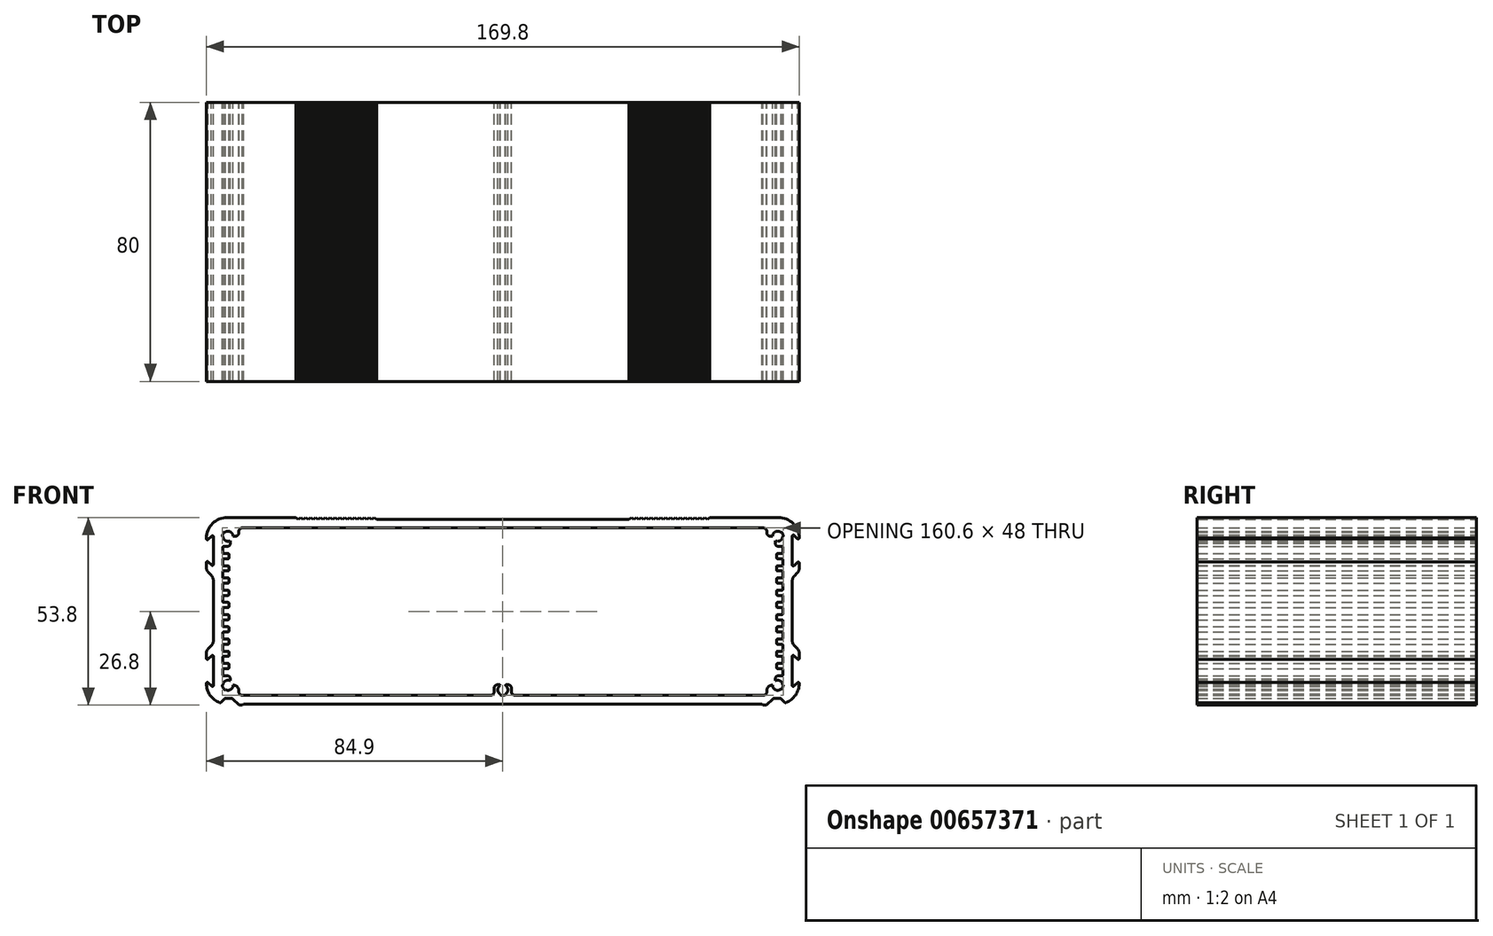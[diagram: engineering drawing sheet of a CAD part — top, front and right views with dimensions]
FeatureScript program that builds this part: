
annotation { "Feature Type Name" : "Feature", "Feature Type Description" : "" }
export const myFeature = defineFeature(function(context is Context, id is Id, definition is map)
    precondition{}
    {
        {
            var Q0;
            Q0=qCreatedBy(makeId("Front.planeOp"),FACE);
            var sketch = newSketch(context, id + "F0", { "sketchPlane" : qUnion([Q0])});
            skArc(sketch, "E0", {"start": v(-74.6, 23.9) * mm, "mid": v(-75.3, 23.6) * mm, "end": v(-75.6, 22.9) * mm});
            skLineSegment(sketch, "E1", {"start": v(74.6, 23.9) * mm, "end": v(-74.6, 23.9) * mm});
            skArc(sketch, "E2", {"start": v(75.6, 22.9) * mm, "mid": v(75.3, 23.6) * mm, "end": v(74.6, 23.9) * mm});
            skLineSegment(sketch, "E3", {"start": v(75.6, 22.5) * mm, "end": v(75.6, 22.9) * mm});
            skArc(sketch, "E4", {"start": v(75.6, 22.5) * mm, "mid": v(75.9, 21.8) * mm, "end": v(76.6, 21.5) * mm});
            skLineSegment(sketch, "E5", {"start": v(77.25, 21.5) * mm, "end": v(76.6, 21.5) * mm});
            skArc(sketch, "E6", {"start": v(79.64, 22.6) * mm, "mid": v(78.1, 22.82) * mm, "end": v(77.25, 21.5) * mm});
            skLineSegment(sketch, "E7", {"start": v(79.73, 22.73) * mm, "end": v(79.64, 22.6) * mm});
            skArc(sketch, "E8", {"start": v(80.3, 21.5) * mm, "mid": v(80.15, 22.18) * mm, "end": v(79.73, 22.73) * mm});
            skLineSegment(sketch, "E9", {"start": v(80.15, 21.5) * mm, "end": v(80.3, 21.5) * mm});
            skArc(sketch, "E10", {"start": v(78.03, 20.22) * mm, "mid": v(79.45, 20.26) * mm, "end": v(80.15, 21.5) * mm});
            skLineSegment(sketch, "E11", {"start": v(78.03, 19.52) * mm, "end": v(78.03, 20.22) * mm});
            skArc(sketch, "E12", {"start": v(78.03, 19.52) * mm, "mid": v(78.33, 18.83) * mm, "end": v(79.02, 18.55) * mm});
            skLineSegment(sketch, "E13", {"start": v(79.95, 18.55) * mm, "end": v(79.02, 18.55) * mm});
            skArc(sketch, "E14", {"start": v(80.25, 18.25) * mm, "mid": v(80.16, 18.46) * mm, "end": v(79.95, 18.55) * mm});
            skLineSegment(sketch, "E15", {"start": v(80.25, 16.85) * mm, "end": v(80.25, 18.25) * mm});
            skArc(sketch, "E16", {"start": v(79.95, 16.55) * mm, "mid": v(80.16, 16.64) * mm, "end": v(80.25, 16.85) * mm});
            skLineSegment(sketch, "E17", {"start": v(78.7, 16.55) * mm, "end": v(79.95, 16.55) * mm});
            skArc(sketch, "E18", {"start": v(78.7, 16.55) * mm, "mid": v(78.49, 16.46) * mm, "end": v(78.4, 16.25) * mm});
            skLineSegment(sketch, "E19", {"start": v(78.4, 15.35) * mm, "end": v(78.4, 16.25) * mm});
            skArc(sketch, "E20", {"start": v(78.4, 15.35) * mm, "mid": v(78.49, 15.14) * mm, "end": v(78.7, 15.05) * mm});
            skLineSegment(sketch, "E21", {"start": v(79.95, 15.05) * mm, "end": v(78.7, 15.05) * mm});
            skArc(sketch, "E22", {"start": v(80.25, 14.75) * mm, "mid": v(80.16, 14.96) * mm, "end": v(79.95, 15.05) * mm});
            skLineSegment(sketch, "E23", {"start": v(80.25, 13.35) * mm, "end": v(80.25, 14.75) * mm});
            skArc(sketch, "E24", {"start": v(79.95, 13.05) * mm, "mid": v(80.16, 13.14) * mm, "end": v(80.25, 13.35) * mm});
            skLineSegment(sketch, "E25", {"start": v(78.7, 13.05) * mm, "end": v(79.95, 13.05) * mm});
            skArc(sketch, "E26", {"start": v(78.7, 13.05) * mm, "mid": v(78.49, 12.96) * mm, "end": v(78.4, 12.75) * mm});
            skLineSegment(sketch, "E27", {"start": v(78.4, 11.85) * mm, "end": v(78.4, 12.75) * mm});
            skArc(sketch, "E28", {"start": v(78.4, 11.85) * mm, "mid": v(78.49, 11.64) * mm, "end": v(78.7, 11.55) * mm});
            skLineSegment(sketch, "E29", {"start": v(79.95, 11.55) * mm, "end": v(78.7, 11.55) * mm});
            skArc(sketch, "E30", {"start": v(80.25, 11.25) * mm, "mid": v(80.16, 11.46) * mm, "end": v(79.95, 11.55) * mm});
            skLineSegment(sketch, "E31", {"start": v(80.25, 9.85) * mm, "end": v(80.25, 11.25) * mm});
            skArc(sketch, "E32", {"start": v(79.95, 9.55) * mm, "mid": v(80.16, 9.64) * mm, "end": v(80.25, 9.85) * mm});
            skLineSegment(sketch, "E33", {"start": v(78.7, 9.55) * mm, "end": v(79.95, 9.55) * mm});
            skArc(sketch, "E34", {"start": v(78.7, 9.55) * mm, "mid": v(78.49, 9.46) * mm, "end": v(78.4, 9.25) * mm});
            skLineSegment(sketch, "E35", {"start": v(78.4, 8.35) * mm, "end": v(78.4, 9.25) * mm});
            skArc(sketch, "E36", {"start": v(78.4, 8.35) * mm, "mid": v(78.49, 8.14) * mm, "end": v(78.7, 8.05) * mm});
            skLineSegment(sketch, "E37", {"start": v(79.95, 8.05) * mm, "end": v(78.7, 8.05) * mm});
            skArc(sketch, "E38", {"start": v(80.25, 7.75) * mm, "mid": v(80.16, 7.96) * mm, "end": v(79.95, 8.05) * mm});
            skLineSegment(sketch, "E39", {"start": v(80.25, 6.35) * mm, "end": v(80.25, 7.75) * mm});
            skArc(sketch, "E40", {"start": v(79.95, 6.05) * mm, "mid": v(80.16, 6.14) * mm, "end": v(80.25, 6.35) * mm});
            skLineSegment(sketch, "E41", {"start": v(78.7, 6.05) * mm, "end": v(79.95, 6.05) * mm});
            skArc(sketch, "E42", {"start": v(78.7, 6.05) * mm, "mid": v(78.49, 5.96) * mm, "end": v(78.4, 5.75) * mm});
            skLineSegment(sketch, "E43", {"start": v(78.4, 4.85) * mm, "end": v(78.4, 5.75) * mm});
            skArc(sketch, "E44", {"start": v(78.4, 4.85) * mm, "mid": v(78.49, 4.64) * mm, "end": v(78.7, 4.55) * mm});
            skLineSegment(sketch, "E45", {"start": v(79.95, 4.55) * mm, "end": v(78.7, 4.55) * mm});
            skArc(sketch, "E46", {"start": v(80.25, 4.25) * mm, "mid": v(80.16, 4.46) * mm, "end": v(79.95, 4.55) * mm});
            skLineSegment(sketch, "E47", {"start": v(80.25, 2.85) * mm, "end": v(80.25, 4.25) * mm});
            skArc(sketch, "E48", {"start": v(79.95, 2.55) * mm, "mid": v(80.16, 2.64) * mm, "end": v(80.25, 2.85) * mm});
            skLineSegment(sketch, "E49", {"start": v(78.7, 2.55) * mm, "end": v(79.95, 2.55) * mm});
            skArc(sketch, "E50", {"start": v(78.7, 2.55) * mm, "mid": v(78.49, 2.46) * mm, "end": v(78.4, 2.25) * mm});
            skLineSegment(sketch, "E51", {"start": v(78.4, 1.35) * mm, "end": v(78.4, 2.25) * mm});
            skArc(sketch, "E52", {"start": v(78.4, 1.35) * mm, "mid": v(78.49, 1.14) * mm, "end": v(78.7, 1.05) * mm});
            skLineSegment(sketch, "E53", {"start": v(79.95, 1.05) * mm, "end": v(78.7, 1.05) * mm});
            skArc(sketch, "E54", {"start": v(80.25, 0.75) * mm, "mid": v(80.16, 0.96) * mm, "end": v(79.95, 1.05) * mm});
            skLineSegment(sketch, "E55", {"start": v(80.25, -0.65) * mm, "end": v(80.25, 0.75) * mm});
            skArc(sketch, "E56", {"start": v(79.95, -0.95) * mm, "mid": v(80.16, -0.86) * mm, "end": v(80.25, -0.65) * mm});
            skLineSegment(sketch, "E57", {"start": v(78.7, -0.95) * mm, "end": v(79.95, -0.95) * mm});
            skArc(sketch, "E58", {"start": v(78.7, -0.95) * mm, "mid": v(78.49, -1.04) * mm, "end": v(78.4, -1.25) * mm});
            skLineSegment(sketch, "E59", {"start": v(78.4, -2.15) * mm, "end": v(78.4, -1.25) * mm});
            skArc(sketch, "E60", {"start": v(78.4, -2.15) * mm, "mid": v(78.49, -2.36) * mm, "end": v(78.7, -2.45) * mm});
            skLineSegment(sketch, "E61", {"start": v(79.95, -2.45) * mm, "end": v(78.7, -2.45) * mm});
            skArc(sketch, "E62", {"start": v(80.25, -2.75) * mm, "mid": v(80.16, -2.54) * mm, "end": v(79.95, -2.45) * mm});
            skLineSegment(sketch, "E63", {"start": v(80.25, -4.15) * mm, "end": v(80.25, -2.75) * mm});
            skArc(sketch, "E64", {"start": v(79.95, -4.45) * mm, "mid": v(80.16, -4.36) * mm, "end": v(80.25, -4.15) * mm});
            skLineSegment(sketch, "E65", {"start": v(78.7, -4.45) * mm, "end": v(79.95, -4.45) * mm});
            skArc(sketch, "E66", {"start": v(78.7, -4.45) * mm, "mid": v(78.49, -4.54) * mm, "end": v(78.4, -4.75) * mm});
            skLineSegment(sketch, "E67", {"start": v(78.4, -5.65) * mm, "end": v(78.4, -4.75) * mm});
            skArc(sketch, "E68", {"start": v(78.4, -5.65) * mm, "mid": v(78.49, -5.86) * mm, "end": v(78.7, -5.95) * mm});
            skLineSegment(sketch, "E69", {"start": v(79.95, -5.95) * mm, "end": v(78.7, -5.95) * mm});
            skArc(sketch, "E70", {"start": v(80.25, -6.25) * mm, "mid": v(80.16, -6.04) * mm, "end": v(79.95, -5.95) * mm});
            skLineSegment(sketch, "E71", {"start": v(80.25, -7.65) * mm, "end": v(80.25, -6.25) * mm});
            skArc(sketch, "E72", {"start": v(79.95, -7.95) * mm, "mid": v(80.16, -7.86) * mm, "end": v(80.25, -7.65) * mm});
            skLineSegment(sketch, "E73", {"start": v(78.7, -7.95) * mm, "end": v(79.95, -7.95) * mm});
            skArc(sketch, "E74", {"start": v(78.7, -7.95) * mm, "mid": v(78.49, -8.04) * mm, "end": v(78.4, -8.25) * mm});
            skLineSegment(sketch, "E75", {"start": v(78.4, -9.15) * mm, "end": v(78.4, -8.25) * mm});
            skArc(sketch, "E76", {"start": v(78.4, -9.15) * mm, "mid": v(78.49, -9.36) * mm, "end": v(78.7, -9.45) * mm});
            skLineSegment(sketch, "E77", {"start": v(79.95, -9.45) * mm, "end": v(78.7, -9.45) * mm});
            skArc(sketch, "E78", {"start": v(80.25, -9.75) * mm, "mid": v(80.16, -9.54) * mm, "end": v(79.95, -9.45) * mm});
            skLineSegment(sketch, "E79", {"start": v(80.25, -11.15) * mm, "end": v(80.25, -9.75) * mm});
            skArc(sketch, "E80", {"start": v(79.95, -11.45) * mm, "mid": v(80.16, -11.36) * mm, "end": v(80.25, -11.15) * mm});
            skLineSegment(sketch, "E81", {"start": v(78.7, -11.45) * mm, "end": v(79.95, -11.45) * mm});
            skArc(sketch, "E82", {"start": v(78.7, -11.45) * mm, "mid": v(78.49, -11.54) * mm, "end": v(78.4, -11.75) * mm});
            skLineSegment(sketch, "E83", {"start": v(78.4, -12.65) * mm, "end": v(78.4, -11.75) * mm});
            skArc(sketch, "E84", {"start": v(78.4, -12.65) * mm, "mid": v(78.49, -12.86) * mm, "end": v(78.7, -12.95) * mm});
            skLineSegment(sketch, "E85", {"start": v(79.95, -12.95) * mm, "end": v(78.7, -12.95) * mm});
            skArc(sketch, "E86", {"start": v(80.25, -13.25) * mm, "mid": v(80.16, -13.04) * mm, "end": v(79.95, -12.95) * mm});
            skLineSegment(sketch, "E87", {"start": v(80.25, -14.65) * mm, "end": v(80.25, -13.25) * mm});
            skArc(sketch, "E88", {"start": v(79.95, -14.95) * mm, "mid": v(80.16, -14.86) * mm, "end": v(80.25, -14.65) * mm});
            skLineSegment(sketch, "E89", {"start": v(78.7, -14.95) * mm, "end": v(79.95, -14.95) * mm});
            skArc(sketch, "E90", {"start": v(78.7, -14.95) * mm, "mid": v(78.49, -15.04) * mm, "end": v(78.4, -15.25) * mm});
            skLineSegment(sketch, "E91", {"start": v(78.4, -16.15) * mm, "end": v(78.4, -15.25) * mm});
            skArc(sketch, "E92", {"start": v(78.4, -16.15) * mm, "mid": v(78.49, -16.36) * mm, "end": v(78.7, -16.45) * mm});
            skLineSegment(sketch, "E93", {"start": v(79.95, -16.45) * mm, "end": v(78.7, -16.45) * mm});
            skArc(sketch, "E94", {"start": v(80.25, -16.75) * mm, "mid": v(80.16, -16.54) * mm, "end": v(79.95, -16.45) * mm});
            skLineSegment(sketch, "E95", {"start": v(80.25, -18.15) * mm, "end": v(80.25, -16.75) * mm});
            skArc(sketch, "E96", {"start": v(79.95, -18.45) * mm, "mid": v(80.16, -18.36) * mm, "end": v(80.25, -18.15) * mm});
            skLineSegment(sketch, "E97", {"start": v(79.02, -18.45) * mm, "end": v(79.95, -18.45) * mm});
            skArc(sketch, "E98", {"start": v(79.02, -18.45) * mm, "mid": v(78.33, -18.73) * mm, "end": v(78.03, -19.42) * mm});
            skLineSegment(sketch, "E99", {"start": v(78.03, -19.92) * mm, "end": v(78.03, -19.42) * mm});
            skArc(sketch, "E100", {"start": v(80.15, -21.2) * mm, "mid": v(79.45, -19.96) * mm, "end": v(78.03, -19.92) * mm});
            skLineSegment(sketch, "E101", {"start": v(80.3, -21.2) * mm, "end": v(80.15, -21.2) * mm});
            skArc(sketch, "E102", {"start": v(79.8, -22.37) * mm, "mid": v(80.17, -21.84) * mm, "end": v(80.3, -21.2) * mm});
            skLineSegment(sketch, "E103", {"start": v(79.7, -22.25) * mm, "end": v(79.8, -22.37) * mm});
            skArc(sketch, "E104", {"start": v(77.25, -21.2) * mm, "mid": v(78.13, -22.53) * mm, "end": v(79.7, -22.25) * mm});
            skLineSegment(sketch, "E105", {"start": v(77.1, -21.2) * mm, "end": v(77.25, -21.2) * mm});
            skArc(sketch, "E106", {"start": v(77.1, -21.2) * mm, "mid": v(76.04, -21.64) * mm, "end": v(75.6, -22.7) * mm});
            skLineSegment(sketch, "E107", {"start": v(75.6, -23.1) * mm, "end": v(75.6, -22.7) * mm});
            skArc(sketch, "E108", {"start": v(74.6, -24.1) * mm, "mid": v(75.3, -23.8) * mm, "end": v(75.6, -23.1) * mm});
            skLineSegment(sketch, "E109", {"start": v(3.5, -24.1) * mm, "end": v(74.6, -24.1) * mm});
            skArc(sketch, "E110", {"start": v(2.5, -23.1) * mm, "mid": v(2.8, -23.8) * mm, "end": v(3.5, -24.1) * mm});
            skLineSegment(sketch, "E111", {"start": v(2.5, -22.05) * mm, "end": v(2.5, -23.1) * mm});
            skArc(sketch, "E112", {"start": v(2.5, -22.05) * mm, "mid": v(2.2, -21.34) * mm, "end": v(1.5, -21.05) * mm});
            skLineSegment(sketch, "E113", {"start": v(0.9, -21.05) * mm, "end": v(1.5, -21.05) * mm});
            skArc(sketch, "E114", {"start": v(0.9, -21.05) * mm, "mid": v(0.85, -21.06) * mm, "end": v(0.8, -21.1) * mm});
            skLineSegment(sketch, "E115", {"start": v(0.73, -21.24) * mm, "end": v(0.8, -21.1) * mm});
            skArc(sketch, "E116", {"start": v(0.72, -23.76) * mm, "mid": v(1.45, -22.5) * mm, "end": v(0.72, -21.24) * mm});
            skLineSegment(sketch, "E117", {"start": v(0.8, -23.89) * mm, "end": v(0.73, -23.76) * mm});
            skArc(sketch, "E118", {"start": v(-0.8, -23.89) * mm, "mid": v(0, -24.1) * mm, "end": v(0.8, -23.89) * mm});
            skLineSegment(sketch, "E119", {"start": v(-0.72, -23.76) * mm, "end": v(-0.8, -23.89) * mm});
            skArc(sketch, "E120", {"start": v(-0.72, -21.24) * mm, "mid": v(-1.45, -22.5) * mm, "end": v(-0.72, -23.76) * mm});
            skLineSegment(sketch, "E121", {"start": v(-0.8, -21.1) * mm, "end": v(-0.72, -21.24) * mm});
            skArc(sketch, "E122", {"start": v(-0.8, -21.1) * mm, "mid": v(-0.85, -21.06) * mm, "end": v(-0.9, -21.05) * mm});
            skLineSegment(sketch, "E123", {"start": v(-1.5, -21.05) * mm, "end": v(-0.9, -21.05) * mm});
            skArc(sketch, "E124", {"start": v(-1.5, -21.05) * mm, "mid": v(-2.2, -21.34) * mm, "end": v(-2.5, -22.05) * mm});
            skLineSegment(sketch, "E125", {"start": v(-2.5, -23.1) * mm, "end": v(-2.5, -22.05) * mm});
            skArc(sketch, "E126", {"start": v(-3.5, -24.1) * mm, "mid": v(-2.8, -23.8) * mm, "end": v(-2.5, -23.1) * mm});
            skLineSegment(sketch, "E127", {"start": v(-74.6, -24.1) * mm, "end": v(-3.5, -24.1) * mm});
            skArc(sketch, "E128", {"start": v(-75.6, -23.1) * mm, "mid": v(-75.3, -23.8) * mm, "end": v(-74.6, -24.1) * mm});
            skLineSegment(sketch, "E129", {"start": v(-75.6, -22.7) * mm, "end": v(-75.6, -23.1) * mm});
            skArc(sketch, "E130", {"start": v(-75.6, -22.7) * mm, "mid": v(-76.04, -21.64) * mm, "end": v(-77.1, -21.2) * mm});
            skLineSegment(sketch, "E131", {"start": v(-77.25, -21.2) * mm, "end": v(-77.1, -21.2) * mm});
            skArc(sketch, "E132", {"start": v(-79.37, -22.48) * mm, "mid": v(-77.95, -22.44) * mm, "end": v(-77.25, -21.2) * mm});
            skLineSegment(sketch, "E133", {"start": v(-79.44, -22.62) * mm, "end": v(-79.37, -22.48) * mm});
            skArc(sketch, "E134", {"start": v(-80.3, -21.2) * mm, "mid": v(-80.07, -22.03) * mm, "end": v(-79.44, -22.62) * mm});
            skLineSegment(sketch, "E135", {"start": v(-80.15, -21.2) * mm, "end": v(-80.3, -21.2) * mm});
            skArc(sketch, "E136", {"start": v(-78.03, -19.92) * mm, "mid": v(-79.45, -19.96) * mm, "end": v(-80.15, -21.2) * mm});
            skLineSegment(sketch, "E137", {"start": v(-78.03, -19.42) * mm, "end": v(-78.03, -19.92) * mm});
            skArc(sketch, "E138", {"start": v(-78.03, -19.42) * mm, "mid": v(-78.33, -18.73) * mm, "end": v(-79.02, -18.45) * mm});
            skLineSegment(sketch, "E139", {"start": v(-79.95, -18.45) * mm, "end": v(-79.02, -18.45) * mm});
            skArc(sketch, "E140", {"start": v(-80.25, -18.15) * mm, "mid": v(-80.16, -18.36) * mm, "end": v(-79.95, -18.45) * mm});
            skLineSegment(sketch, "E141", {"start": v(-80.25, -16.75) * mm, "end": v(-80.25, -18.15) * mm});
            skArc(sketch, "E142", {"start": v(-79.95, -16.45) * mm, "mid": v(-80.16, -16.54) * mm, "end": v(-80.25, -16.75) * mm});
            skLineSegment(sketch, "E143", {"start": v(-78.7, -16.45) * mm, "end": v(-79.95, -16.45) * mm});
            skArc(sketch, "E144", {"start": v(-78.7, -16.45) * mm, "mid": v(-78.49, -16.36) * mm, "end": v(-78.4, -16.15) * mm});
            skLineSegment(sketch, "E145", {"start": v(-78.4, -15.25) * mm, "end": v(-78.4, -16.15) * mm});
            skArc(sketch, "E146", {"start": v(-78.4, -15.25) * mm, "mid": v(-78.49, -15.04) * mm, "end": v(-78.7, -14.95) * mm});
            skLineSegment(sketch, "E147", {"start": v(-79.95, -14.95) * mm, "end": v(-78.7, -14.95) * mm});
            skArc(sketch, "E148", {"start": v(-80.25, -14.65) * mm, "mid": v(-80.16, -14.86) * mm, "end": v(-79.95, -14.95) * mm});
            skLineSegment(sketch, "E149", {"start": v(-80.25, -13.25) * mm, "end": v(-80.25, -14.65) * mm});
            skArc(sketch, "E150", {"start": v(-79.95, -12.95) * mm, "mid": v(-80.16, -13.04) * mm, "end": v(-80.25, -13.25) * mm});
            skLineSegment(sketch, "E151", {"start": v(-78.7, -12.95) * mm, "end": v(-79.95, -12.95) * mm});
            skArc(sketch, "E152", {"start": v(-78.7, -12.95) * mm, "mid": v(-78.49, -12.86) * mm, "end": v(-78.4, -12.65) * mm});
            skLineSegment(sketch, "E153", {"start": v(-78.4, -11.75) * mm, "end": v(-78.4, -12.65) * mm});
            skArc(sketch, "E154", {"start": v(-78.4, -11.75) * mm, "mid": v(-78.49, -11.54) * mm, "end": v(-78.7, -11.45) * mm});
            skLineSegment(sketch, "E155", {"start": v(-79.95, -11.45) * mm, "end": v(-78.7, -11.45) * mm});
            skArc(sketch, "E156", {"start": v(-80.25, -11.15) * mm, "mid": v(-80.16, -11.36) * mm, "end": v(-79.95, -11.45) * mm});
            skLineSegment(sketch, "E157", {"start": v(-80.25, -9.75) * mm, "end": v(-80.25, -11.15) * mm});
            skArc(sketch, "E158", {"start": v(-79.95, -9.45) * mm, "mid": v(-80.16, -9.54) * mm, "end": v(-80.25, -9.75) * mm});
            skLineSegment(sketch, "E159", {"start": v(-78.7, -9.45) * mm, "end": v(-79.95, -9.45) * mm});
            skArc(sketch, "E160", {"start": v(-78.7, -9.45) * mm, "mid": v(-78.49, -9.36) * mm, "end": v(-78.4, -9.15) * mm});
            skLineSegment(sketch, "E161", {"start": v(-78.4, -8.25) * mm, "end": v(-78.4, -9.15) * mm});
            skArc(sketch, "E162", {"start": v(-78.4, -8.25) * mm, "mid": v(-78.49, -8.04) * mm, "end": v(-78.7, -7.95) * mm});
            skLineSegment(sketch, "E163", {"start": v(-79.95, -7.95) * mm, "end": v(-78.7, -7.95) * mm});
            skArc(sketch, "E164", {"start": v(-80.25, -7.65) * mm, "mid": v(-80.16, -7.86) * mm, "end": v(-79.95, -7.95) * mm});
            skLineSegment(sketch, "E165", {"start": v(-80.25, -6.25) * mm, "end": v(-80.25, -7.65) * mm});
            skArc(sketch, "E166", {"start": v(-79.95, -5.95) * mm, "mid": v(-80.16, -6.04) * mm, "end": v(-80.25, -6.25) * mm});
            skLineSegment(sketch, "E167", {"start": v(-78.7, -5.95) * mm, "end": v(-79.95, -5.95) * mm});
            skArc(sketch, "E168", {"start": v(-78.7, -5.95) * mm, "mid": v(-78.49, -5.86) * mm, "end": v(-78.4, -5.65) * mm});
            skLineSegment(sketch, "E169", {"start": v(-78.4, -4.75) * mm, "end": v(-78.4, -5.65) * mm});
            skArc(sketch, "E170", {"start": v(-78.4, -4.75) * mm, "mid": v(-78.49, -4.54) * mm, "end": v(-78.7, -4.45) * mm});
            skLineSegment(sketch, "E171", {"start": v(-79.95, -4.45) * mm, "end": v(-78.7, -4.45) * mm});
            skArc(sketch, "E172", {"start": v(-80.25, -4.15) * mm, "mid": v(-80.16, -4.36) * mm, "end": v(-79.95, -4.45) * mm});
            skLineSegment(sketch, "E173", {"start": v(-80.25, -2.75) * mm, "end": v(-80.25, -4.15) * mm});
            skArc(sketch, "E174", {"start": v(-79.95, -2.45) * mm, "mid": v(-80.16, -2.54) * mm, "end": v(-80.25, -2.75) * mm});
            skLineSegment(sketch, "E175", {"start": v(-78.7, -2.45) * mm, "end": v(-79.95, -2.45) * mm});
            skArc(sketch, "E176", {"start": v(-78.7, -2.45) * mm, "mid": v(-78.49, -2.36) * mm, "end": v(-78.4, -2.15) * mm});
            skLineSegment(sketch, "E177", {"start": v(-78.4, -1.25) * mm, "end": v(-78.4, -2.15) * mm});
            skArc(sketch, "E178", {"start": v(-78.4, -1.25) * mm, "mid": v(-78.49, -1.04) * mm, "end": v(-78.7, -0.95) * mm});
            skLineSegment(sketch, "E179", {"start": v(-79.95, -0.95) * mm, "end": v(-78.7, -0.95) * mm});
            skArc(sketch, "E180", {"start": v(-80.25, -0.65) * mm, "mid": v(-80.16, -0.86) * mm, "end": v(-79.95, -0.95) * mm});
            skLineSegment(sketch, "E181", {"start": v(-80.25, 0.75) * mm, "end": v(-80.25, -0.65) * mm});
            skArc(sketch, "E182", {"start": v(-79.95, 1.05) * mm, "mid": v(-80.16, 0.96) * mm, "end": v(-80.25, 0.75) * mm});
            skLineSegment(sketch, "E183", {"start": v(-78.7, 1.05) * mm, "end": v(-79.95, 1.05) * mm});
            skArc(sketch, "E184", {"start": v(-78.7, 1.05) * mm, "mid": v(-78.49, 1.14) * mm, "end": v(-78.4, 1.35) * mm});
            skLineSegment(sketch, "E185", {"start": v(-78.4, 2.25) * mm, "end": v(-78.4, 1.35) * mm});
            skArc(sketch, "E186", {"start": v(-78.4, 2.25) * mm, "mid": v(-78.49, 2.46) * mm, "end": v(-78.7, 2.55) * mm});
            skLineSegment(sketch, "E187", {"start": v(-79.95, 2.55) * mm, "end": v(-78.7, 2.55) * mm});
            skArc(sketch, "E188", {"start": v(-80.25, 2.85) * mm, "mid": v(-80.16, 2.64) * mm, "end": v(-79.95, 2.55) * mm});
            skLineSegment(sketch, "E189", {"start": v(-80.25, 4.25) * mm, "end": v(-80.25, 2.85) * mm});
            skArc(sketch, "E190", {"start": v(-79.95, 4.55) * mm, "mid": v(-80.16, 4.46) * mm, "end": v(-80.25, 4.25) * mm});
            skLineSegment(sketch, "E191", {"start": v(-78.7, 4.55) * mm, "end": v(-79.95, 4.55) * mm});
            skArc(sketch, "E192", {"start": v(-78.7, 4.55) * mm, "mid": v(-78.49, 4.64) * mm, "end": v(-78.4, 4.85) * mm});
            skLineSegment(sketch, "E193", {"start": v(-78.4, 5.75) * mm, "end": v(-78.4, 4.85) * mm});
            skArc(sketch, "E194", {"start": v(-78.4, 5.75) * mm, "mid": v(-78.49, 5.96) * mm, "end": v(-78.7, 6.05) * mm});
            skLineSegment(sketch, "E195", {"start": v(-79.95, 6.05) * mm, "end": v(-78.7, 6.05) * mm});
            skArc(sketch, "E196", {"start": v(-80.25, 6.35) * mm, "mid": v(-80.16, 6.14) * mm, "end": v(-79.95, 6.05) * mm});
            skLineSegment(sketch, "E197", {"start": v(-80.25, 7.75) * mm, "end": v(-80.25, 6.35) * mm});
            skArc(sketch, "E198", {"start": v(-79.95, 8.05) * mm, "mid": v(-80.16, 7.96) * mm, "end": v(-80.25, 7.75) * mm});
            skLineSegment(sketch, "E199", {"start": v(-78.7, 8.05) * mm, "end": v(-79.95, 8.05) * mm});
            skArc(sketch, "E200", {"start": v(-78.7, 8.05) * mm, "mid": v(-78.49, 8.14) * mm, "end": v(-78.4, 8.35) * mm});
            skLineSegment(sketch, "E201", {"start": v(-78.4, 9.25) * mm, "end": v(-78.4, 8.35) * mm});
            skArc(sketch, "E202", {"start": v(-78.4, 9.25) * mm, "mid": v(-78.49, 9.46) * mm, "end": v(-78.7, 9.55) * mm});
            skLineSegment(sketch, "E203", {"start": v(-79.95, 9.55) * mm, "end": v(-78.7, 9.55) * mm});
            skArc(sketch, "E204", {"start": v(-80.25, 9.85) * mm, "mid": v(-80.16, 9.64) * mm, "end": v(-79.95, 9.55) * mm});
            skLineSegment(sketch, "E205", {"start": v(-80.25, 11.25) * mm, "end": v(-80.25, 9.85) * mm});
            skArc(sketch, "E206", {"start": v(-79.95, 11.55) * mm, "mid": v(-80.16, 11.46) * mm, "end": v(-80.25, 11.25) * mm});
            skLineSegment(sketch, "E207", {"start": v(-78.7, 11.55) * mm, "end": v(-79.95, 11.55) * mm});
            skArc(sketch, "E208", {"start": v(-78.7, 11.55) * mm, "mid": v(-78.49, 11.64) * mm, "end": v(-78.4, 11.85) * mm});
            skLineSegment(sketch, "E209", {"start": v(-78.4, 12.75) * mm, "end": v(-78.4, 11.85) * mm});
            skArc(sketch, "E210", {"start": v(-78.4, 12.75) * mm, "mid": v(-78.49, 12.96) * mm, "end": v(-78.7, 13.05) * mm});
            skLineSegment(sketch, "E211", {"start": v(-79.95, 13.05) * mm, "end": v(-78.7, 13.05) * mm});
            skArc(sketch, "E212", {"start": v(-80.25, 13.35) * mm, "mid": v(-80.16, 13.14) * mm, "end": v(-79.95, 13.05) * mm});
            skLineSegment(sketch, "E213", {"start": v(-80.25, 14.75) * mm, "end": v(-80.25, 13.35) * mm});
            skArc(sketch, "E214", {"start": v(-79.95, 15.05) * mm, "mid": v(-80.16, 14.96) * mm, "end": v(-80.25, 14.75) * mm});
            skLineSegment(sketch, "E215", {"start": v(-78.7, 15.05) * mm, "end": v(-79.95, 15.05) * mm});
            skArc(sketch, "E216", {"start": v(-78.7, 15.05) * mm, "mid": v(-78.49, 15.14) * mm, "end": v(-78.4, 15.35) * mm});
            skLineSegment(sketch, "E217", {"start": v(-78.4, 16.25) * mm, "end": v(-78.4, 15.35) * mm});
            skArc(sketch, "E218", {"start": v(-78.4, 16.25) * mm, "mid": v(-78.49, 16.46) * mm, "end": v(-78.7, 16.55) * mm});
            skLineSegment(sketch, "E219", {"start": v(-79.95, 16.55) * mm, "end": v(-78.7, 16.55) * mm});
            skArc(sketch, "E220", {"start": v(-80.25, 16.85) * mm, "mid": v(-80.16, 16.64) * mm, "end": v(-79.95, 16.55) * mm});
            skLineSegment(sketch, "E221", {"start": v(-80.25, 18.25) * mm, "end": v(-80.25, 16.85) * mm});
            skArc(sketch, "E222", {"start": v(-79.95, 18.55) * mm, "mid": v(-80.16, 18.46) * mm, "end": v(-80.25, 18.25) * mm});
            skLineSegment(sketch, "E223", {"start": v(-79.02, 18.55) * mm, "end": v(-79.95, 18.55) * mm});
            skArc(sketch, "E224", {"start": v(-79.02, 18.55) * mm, "mid": v(-78.33, 18.83) * mm, "end": v(-78.03, 19.52) * mm});
            skLineSegment(sketch, "E225", {"start": v(-78.03, 20.22) * mm, "end": v(-78.03, 19.52) * mm});
            skArc(sketch, "E226", {"start": v(-80.15, 21.5) * mm, "mid": v(-79.45, 20.26) * mm, "end": v(-78.03, 20.22) * mm});
            skLineSegment(sketch, "E227", {"start": v(-80.3, 21.5) * mm, "end": v(-80.15, 21.5) * mm});
            skArc(sketch, "E228", {"start": v(-79.73, 22.73) * mm, "mid": v(-80.15, 22.18) * mm, "end": v(-80.3, 21.5) * mm});
            skLineSegment(sketch, "E229", {"start": v(-79.64, 22.6) * mm, "end": v(-79.73, 22.73) * mm});
            skArc(sketch, "E230", {"start": v(-77.25, 21.5) * mm, "mid": v(-78.1, 22.82) * mm, "end": v(-79.64, 22.6) * mm});
            skLineSegment(sketch, "E231", {"start": v(-76.6, 21.5) * mm, "end": v(-77.25, 21.5) * mm});
            skArc(sketch, "E232", {"start": v(-76.6, 21.5) * mm, "mid": v(-75.9, 21.8) * mm, "end": v(-75.6, 22.5) * mm});
            skLineSegment(sketch, "E233", {"start": v(-75.6, 22.9) * mm, "end": v(-75.6, 22.5) * mm});
            skLineSegment(sketch, "E234", {"start": v(-36.15, 26.4) * mm, "end": v(-36.85, 26.9) * mm});
            skLineSegment(sketch, "E235", {"start": v(-36.85, 26.9) * mm, "end": v(-37.55, 26.4) * mm});
            skLineSegment(sketch, "E236", {"start": v(-37.55, 26.4) * mm, "end": v(-38.25, 26.9) * mm});
            skLineSegment(sketch, "E237", {"start": v(-38.25, 26.9) * mm, "end": v(-38.95, 26.4) * mm});
            skLineSegment(sketch, "E238", {"start": v(-38.95, 26.4) * mm, "end": v(-39.65, 26.9) * mm});
            skLineSegment(sketch, "E239", {"start": v(-39.65, 26.9) * mm, "end": v(-40.35, 26.4) * mm});
            skLineSegment(sketch, "E240", {"start": v(-40.35, 26.4) * mm, "end": v(-41.05, 26.9) * mm});
            skLineSegment(sketch, "E241", {"start": v(-41.05, 26.9) * mm, "end": v(-41.75, 26.4) * mm});
            skLineSegment(sketch, "E242", {"start": v(-41.75, 26.4) * mm, "end": v(-42.45, 26.9) * mm});
            skLineSegment(sketch, "E243", {"start": v(-42.45, 26.9) * mm, "end": v(-43.15, 26.4) * mm});
            skLineSegment(sketch, "E244", {"start": v(-43.15, 26.4) * mm, "end": v(-43.85, 26.9) * mm});
            skLineSegment(sketch, "E245", {"start": v(-43.85, 26.9) * mm, "end": v(-44.55, 26.4) * mm});
            skLineSegment(sketch, "E246", {"start": v(-44.55, 26.4) * mm, "end": v(-45.25, 26.9) * mm});
            skLineSegment(sketch, "E247", {"start": v(-45.25, 26.9) * mm, "end": v(-45.95, 26.4) * mm});
            skLineSegment(sketch, "E248", {"start": v(-45.95, 26.4) * mm, "end": v(-46.65, 26.9) * mm});
            skLineSegment(sketch, "E249", {"start": v(-46.65, 26.9) * mm, "end": v(-47.35, 26.4) * mm});
            skLineSegment(sketch, "E250", {"start": v(-47.35, 26.4) * mm, "end": v(-48.05, 26.9) * mm});
            skLineSegment(sketch, "E251", {"start": v(-48.05, 26.9) * mm, "end": v(-48.75, 26.4) * mm});
            skLineSegment(sketch, "E252", {"start": v(-48.75, 26.4) * mm, "end": v(-49.45, 26.9) * mm});
            skLineSegment(sketch, "E253", {"start": v(-49.45, 26.9) * mm, "end": v(-50.15, 26.4) * mm});
            skLineSegment(sketch, "E254", {"start": v(-50.15, 26.4) * mm, "end": v(-50.85, 26.9) * mm});
            skLineSegment(sketch, "E255", {"start": v(-50.85, 26.9) * mm, "end": v(-51.55, 26.4) * mm});
            skLineSegment(sketch, "E256", {"start": v(-51.55, 26.4) * mm, "end": v(-52.25, 26.9) * mm});
            skLineSegment(sketch, "E257", {"start": v(-52.25, 26.9) * mm, "end": v(-52.95, 26.4) * mm});
            skLineSegment(sketch, "E258", {"start": v(-52.95, 26.4) * mm, "end": v(-53.65, 26.9) * mm});
            skLineSegment(sketch, "E259", {"start": v(-53.65, 26.9) * mm, "end": v(-54.35, 26.4) * mm});
            skLineSegment(sketch, "E260", {"start": v(-54.35, 26.4) * mm, "end": v(-55.05, 26.9) * mm});
            skLineSegment(sketch, "E261", {"start": v(-55.05, 26.9) * mm, "end": v(-55.75, 26.4) * mm});
            skLineSegment(sketch, "E262", {"start": v(-55.75, 26.4) * mm, "end": v(-56.45, 26.9) * mm});
            skLineSegment(sketch, "E263", {"start": v(-56.45, 26.9) * mm, "end": v(-57.15, 26.4) * mm});
            skLineSegment(sketch, "E264", {"start": v(-57.15, 26.4) * mm, "end": v(-57.85, 26.9) * mm});
            skLineSegment(sketch, "E265", {"start": v(-57.85, 26.9) * mm, "end": v(-58.55, 26.4) * mm});
            skLineSegment(sketch, "E266", {"start": v(-58.55, 26.4) * mm, "end": v(-59.25, 26.9) * mm});
            skLineSegment(sketch, "E267", {"start": v(-59.25, 26.9) * mm, "end": v(-78.9, 26.9) * mm});
            skArc(sketch, "E268", {"start": v(-78.9, 26.9) * mm, "mid": v(-83.14, 25.14) * mm, "end": v(-84.9, 20.9) * mm});
            skLineSegment(sketch, "E269", {"start": v(-84.9, 20.9) * mm, "end": v(-84.9, 20.8) * mm});
            skArc(sketch, "E270", {"start": v(-84.9, 20.8) * mm, "mid": v(-84.71, 20.52) * mm, "end": v(-84.39, 20.59) * mm});
            skLineSegment(sketch, "E271", {"start": v(-84.39, 20.59) * mm, "end": v(-83.41, 21.56) * mm});
            skArc(sketch, "E272", {"start": v(-82.9, 21.35) * mm, "mid": v(-83.09, 21.63) * mm, "end": v(-83.41, 21.56) * mm});
            skLineSegment(sketch, "E273", {"start": v(-82.9, 21.35) * mm, "end": v(-82.9, 13.45) * mm});
            skArc(sketch, "E274", {"start": v(-83.41, 13.24) * mm, "mid": v(-83.09, 13.17) * mm, "end": v(-82.9, 13.45) * mm});
            skLineSegment(sketch, "E275", {"start": v(-83.41, 13.24) * mm, "end": v(-84.39, 14.21) * mm});
            skArc(sketch, "E276", {"start": v(-84.39, 14.21) * mm, "mid": v(-84.71, 14.28) * mm, "end": v(-84.9, 14) * mm});
            skLineSegment(sketch, "E277", {"start": v(-84.9, 14) * mm, "end": v(-84.9, 12.55) * mm});
            skArc(sketch, "E278", {"start": v(-84.9, 12.55) * mm, "mid": v(-84.75, 11.79) * mm, "end": v(-84.31, 11.14) * mm});
            skLineSegment(sketch, "E279", {"start": v(-84.31, 11.14) * mm, "end": v(-83.49, 10.31) * mm});
            skArc(sketch, "E280", {"start": v(-82.9, 8.7) * mm, "mid": v(-83.05, 9.56) * mm, "end": v(-83.49, 10.31) * mm});
            skLineSegment(sketch, "E281", {"start": v(-82.9, 8.7) * mm, "end": v(-82.9, -8.4) * mm});
            skArc(sketch, "E282", {"start": v(-83.49, -9.81) * mm, "mid": v(-83.05, -9.16) * mm, "end": v(-82.9, -8.4) * mm});
            skLineSegment(sketch, "E283", {"start": v(-83.49, -9.81) * mm, "end": v(-84.31, -10.64) * mm});
            skArc(sketch, "E284", {"start": v(-84.31, -10.64) * mm, "mid": v(-84.75, -11.29) * mm, "end": v(-84.9, -12.05) * mm});
            skLineSegment(sketch, "E285", {"start": v(-84.9, -12.05) * mm, "end": v(-84.9, -13.5) * mm});
            skArc(sketch, "E286", {"start": v(-84.9, -13.5) * mm, "mid": v(-84.71, -13.78) * mm, "end": v(-84.39, -13.71) * mm});
            skLineSegment(sketch, "E287", {"start": v(-84.39, -13.71) * mm, "end": v(-83.41, -12.74) * mm});
            skArc(sketch, "E288", {"start": v(-82.9, -12.95) * mm, "mid": v(-83.09, -12.67) * mm, "end": v(-83.41, -12.74) * mm});
            skLineSegment(sketch, "E289", {"start": v(-82.9, -12.95) * mm, "end": v(-82.9, -21.25) * mm});
            skArc(sketch, "E290", {"start": v(-83.41, -21.46) * mm, "mid": v(-83.09, -21.53) * mm, "end": v(-82.9, -21.25) * mm});
            skLineSegment(sketch, "E291", {"start": v(-83.41, -21.46) * mm, "end": v(-84.39, -20.49) * mm});
            skArc(sketch, "E292", {"start": v(-84.39, -20.49) * mm, "mid": v(-84.71, -20.4) * mm, "end": v(-84.9, -20.68) * mm});
            skArc(sketch, "E293", {"start": v(-84.9, -20.68) * mm, "mid": v(-83.83, -24.02) * mm, "end": v(-81.09, -26.19) * mm});
            skArc(sketch, "E294", {"start": v(-81.09, -26.19) * mm, "mid": v(-80.92, -26.2) * mm, "end": v(-80.77, -26.12) * mm});
            skLineSegment(sketch, "E295", {"start": v(-80.77, -26.12) * mm, "end": v(-79.73, -25.09) * mm});
            skArc(sketch, "E296", {"start": v(-79.52, -25) * mm, "mid": v(-79.64, -25.02) * mm, "end": v(-79.73, -25.09) * mm});
            skLineSegment(sketch, "E297", {"start": v(-79.52, -25) * mm, "end": v(-77.58, -25) * mm});
            skArc(sketch, "E298", {"start": v(-77.36, -25.09) * mm, "mid": v(-77.46, -25.02) * mm, "end": v(-77.58, -25) * mm});
            skLineSegment(sketch, "E299", {"start": v(-77.36, -25.09) * mm, "end": v(-75.55, -26.9) * mm});
            skLineSegment(sketch, "E300", {"start": v(-75.55, -26.9) * mm, "end": v(-74.55, -26.9) * mm});
            skLineSegment(sketch, "E301", {"start": v(-74.55, -26.9) * mm, "end": v(-74.25, -26.6) * mm});
            skLineSegment(sketch, "E302", {"start": v(-74.25, -26.6) * mm, "end": v(74.25, -26.6) * mm});
            skLineSegment(sketch, "E303", {"start": v(74.25, -26.6) * mm, "end": v(74.55, -26.9) * mm});
            skLineSegment(sketch, "E304", {"start": v(74.55, -26.9) * mm, "end": v(75.55, -26.9) * mm});
            skLineSegment(sketch, "E305", {"start": v(75.55, -26.9) * mm, "end": v(77.36, -25.09) * mm});
            skArc(sketch, "E306", {"start": v(77.58, -25) * mm, "mid": v(77.46, -25.02) * mm, "end": v(77.36, -25.09) * mm});
            skLineSegment(sketch, "E307", {"start": v(77.58, -25) * mm, "end": v(79.52, -25) * mm});
            skArc(sketch, "E308", {"start": v(79.73, -25.09) * mm, "mid": v(79.64, -25.02) * mm, "end": v(79.52, -25) * mm});
            skLineSegment(sketch, "E309", {"start": v(79.73, -25.09) * mm, "end": v(80.77, -26.12) * mm});
            skArc(sketch, "E310", {"start": v(80.77, -26.12) * mm, "mid": v(80.92, -26.2) * mm, "end": v(81.09, -26.19) * mm});
            skArc(sketch, "E311", {"start": v(81.09, -26.19) * mm, "mid": v(83.83, -24.02) * mm, "end": v(84.9, -20.68) * mm});
            skArc(sketch, "E312", {"start": v(84.9, -20.68) * mm, "mid": v(84.71, -20.4) * mm, "end": v(84.39, -20.49) * mm});
            skLineSegment(sketch, "E313", {"start": v(84.39, -20.49) * mm, "end": v(83.41, -21.46) * mm});
            skArc(sketch, "E314", {"start": v(82.9, -21.25) * mm, "mid": v(83.09, -21.53) * mm, "end": v(83.41, -21.46) * mm});
            skLineSegment(sketch, "E315", {"start": v(82.9, -21.25) * mm, "end": v(82.9, -12.95) * mm});
            skArc(sketch, "E316", {"start": v(83.41, -12.74) * mm, "mid": v(83.09, -12.67) * mm, "end": v(82.9, -12.95) * mm});
            skLineSegment(sketch, "E317", {"start": v(83.41, -12.74) * mm, "end": v(84.39, -13.71) * mm});
            skArc(sketch, "E318", {"start": v(84.39, -13.71) * mm, "mid": v(84.71, -13.78) * mm, "end": v(84.9, -13.5) * mm});
            skLineSegment(sketch, "E319", {"start": v(84.9, -13.5) * mm, "end": v(84.9, -12.05) * mm});
            skArc(sketch, "E320", {"start": v(84.9, -12.05) * mm, "mid": v(84.75, -11.29) * mm, "end": v(84.31, -10.64) * mm});
            skLineSegment(sketch, "E321", {"start": v(84.31, -10.64) * mm, "end": v(83.49, -9.81) * mm});
            skArc(sketch, "E322", {"start": v(82.9, -8.4) * mm, "mid": v(83.05, -9.16) * mm, "end": v(83.49, -9.81) * mm});
            skLineSegment(sketch, "E323", {"start": v(82.9, -8.4) * mm, "end": v(82.9, 8.7) * mm});
            skArc(sketch, "E324", {"start": v(83.49, 10.11) * mm, "mid": v(83.05, 9.46) * mm, "end": v(82.9, 8.7) * mm});
            skLineSegment(sketch, "E325", {"start": v(83.49, 10.11) * mm, "end": v(84.31, 10.94) * mm});
            skArc(sketch, "E326", {"start": v(84.31, 10.94) * mm, "mid": v(84.75, 11.59) * mm, "end": v(84.9, 12.35) * mm});
            skLineSegment(sketch, "E327", {"start": v(84.9, 12.35) * mm, "end": v(84.9, 13.8) * mm});
            skArc(sketch, "E328", {"start": v(84.9, 13.8) * mm, "mid": v(84.71, 14.08) * mm, "end": v(84.39, 14.01) * mm});
            skLineSegment(sketch, "E329", {"start": v(84.39, 14.01) * mm, "end": v(83.41, 13.04) * mm});
            skArc(sketch, "E330", {"start": v(82.9, 13.25) * mm, "mid": v(83.09, 12.97) * mm, "end": v(83.41, 13.04) * mm});
            skLineSegment(sketch, "E331", {"start": v(82.9, 13.25) * mm, "end": v(82.9, 21.55) * mm});
            skArc(sketch, "E332", {"start": v(83.41, 21.76) * mm, "mid": v(83.09, 21.83) * mm, "end": v(82.9, 21.55) * mm});
            skLineSegment(sketch, "E333", {"start": v(83.41, 21.76) * mm, "end": v(84.39, 20.79) * mm});
            skArc(sketch, "E334", {"start": v(84.39, 20.79) * mm, "mid": v(84.7, 20.72) * mm, "end": v(84.9, 20.98) * mm});
            skArc(sketch, "E335", {"start": v(84.9, 20.98) * mm, "mid": v(83.11, 25.17) * mm, "end": v(78.9, 26.9) * mm});
            skLineSegment(sketch, "E336", {"start": v(78.9, 26.9) * mm, "end": v(59.25, 26.9) * mm});
            skLineSegment(sketch, "E337", {"start": v(59.25, 26.9) * mm, "end": v(58.55, 26.4) * mm});
            skLineSegment(sketch, "E338", {"start": v(58.55, 26.4) * mm, "end": v(57.85, 26.9) * mm});
            skLineSegment(sketch, "E339", {"start": v(57.85, 26.9) * mm, "end": v(57.15, 26.4) * mm});
            skLineSegment(sketch, "E340", {"start": v(57.15, 26.4) * mm, "end": v(56.45, 26.9) * mm});
            skLineSegment(sketch, "E341", {"start": v(56.45, 26.9) * mm, "end": v(55.75, 26.4) * mm});
            skLineSegment(sketch, "E342", {"start": v(55.75, 26.4) * mm, "end": v(55.05, 26.9) * mm});
            skLineSegment(sketch, "E343", {"start": v(55.05, 26.9) * mm, "end": v(54.35, 26.4) * mm});
            skLineSegment(sketch, "E344", {"start": v(54.35, 26.4) * mm, "end": v(53.65, 26.9) * mm});
            skLineSegment(sketch, "E345", {"start": v(53.65, 26.9) * mm, "end": v(52.95, 26.4) * mm});
            skLineSegment(sketch, "E346", {"start": v(52.95, 26.4) * mm, "end": v(52.25, 26.9) * mm});
            skLineSegment(sketch, "E347", {"start": v(52.25, 26.9) * mm, "end": v(51.55, 26.4) * mm});
            skLineSegment(sketch, "E348", {"start": v(51.55, 26.4) * mm, "end": v(50.85, 26.9) * mm});
            skLineSegment(sketch, "E349", {"start": v(50.85, 26.9) * mm, "end": v(50.15, 26.4) * mm});
            skLineSegment(sketch, "E350", {"start": v(50.15, 26.4) * mm, "end": v(49.45, 26.9) * mm});
            skLineSegment(sketch, "E351", {"start": v(49.45, 26.9) * mm, "end": v(48.75, 26.4) * mm});
            skLineSegment(sketch, "E352", {"start": v(48.75, 26.4) * mm, "end": v(48.05, 26.9) * mm});
            skLineSegment(sketch, "E353", {"start": v(48.05, 26.9) * mm, "end": v(47.35, 26.4) * mm});
            skLineSegment(sketch, "E354", {"start": v(47.35, 26.4) * mm, "end": v(46.65, 26.9) * mm});
            skLineSegment(sketch, "E355", {"start": v(46.65, 26.9) * mm, "end": v(45.95, 26.4) * mm});
            skLineSegment(sketch, "E356", {"start": v(45.95, 26.4) * mm, "end": v(45.25, 26.9) * mm});
            skLineSegment(sketch, "E357", {"start": v(45.25, 26.9) * mm, "end": v(44.55, 26.4) * mm});
            skLineSegment(sketch, "E358", {"start": v(44.55, 26.4) * mm, "end": v(43.85, 26.9) * mm});
            skLineSegment(sketch, "E359", {"start": v(43.85, 26.9) * mm, "end": v(43.15, 26.4) * mm});
            skLineSegment(sketch, "E360", {"start": v(43.15, 26.4) * mm, "end": v(42.45, 26.9) * mm});
            skLineSegment(sketch, "E361", {"start": v(42.45, 26.9) * mm, "end": v(41.75, 26.4) * mm});
            skLineSegment(sketch, "E362", {"start": v(41.75, 26.4) * mm, "end": v(41.05, 26.9) * mm});
            skLineSegment(sketch, "E363", {"start": v(41.05, 26.9) * mm, "end": v(40.35, 26.4) * mm});
            skLineSegment(sketch, "E364", {"start": v(40.35, 26.4) * mm, "end": v(39.65, 26.9) * mm});
            skLineSegment(sketch, "E365", {"start": v(39.65, 26.9) * mm, "end": v(38.95, 26.4) * mm});
            skLineSegment(sketch, "E366", {"start": v(38.95, 26.4) * mm, "end": v(38.25, 26.9) * mm});
            skLineSegment(sketch, "E367", {"start": v(38.25, 26.9) * mm, "end": v(37.55, 26.4) * mm});
            skLineSegment(sketch, "E368", {"start": v(37.55, 26.4) * mm, "end": v(36.85, 26.9) * mm});
            skLineSegment(sketch, "E369", {"start": v(36.85, 26.9) * mm, "end": v(36.15, 26.4) * mm});
            skLineSegment(sketch, "E370", {"start": v(36.15, 26.4) * mm, "end": v(-36.15, 26.4) * mm});
            skSolve(sketch);
        }
        {
            var Q0;
            Q0=makeQuery(id+"F0.imprint","IMPRINT",FACE,{"disambiguationData":[TD([[makeQuery(id+"F0.imprint","IMPRINT",EDGE,{"derivedFrom":sQuery(id+"F0.wireOp",EDGE,"E0")}),-1.0]])]});
            extrude(context, id + "F1", {"entities" : qUnion([Q0]), "depth" : 80 * mm, "offsetDistance" : 25 * mm});
        }
    });
